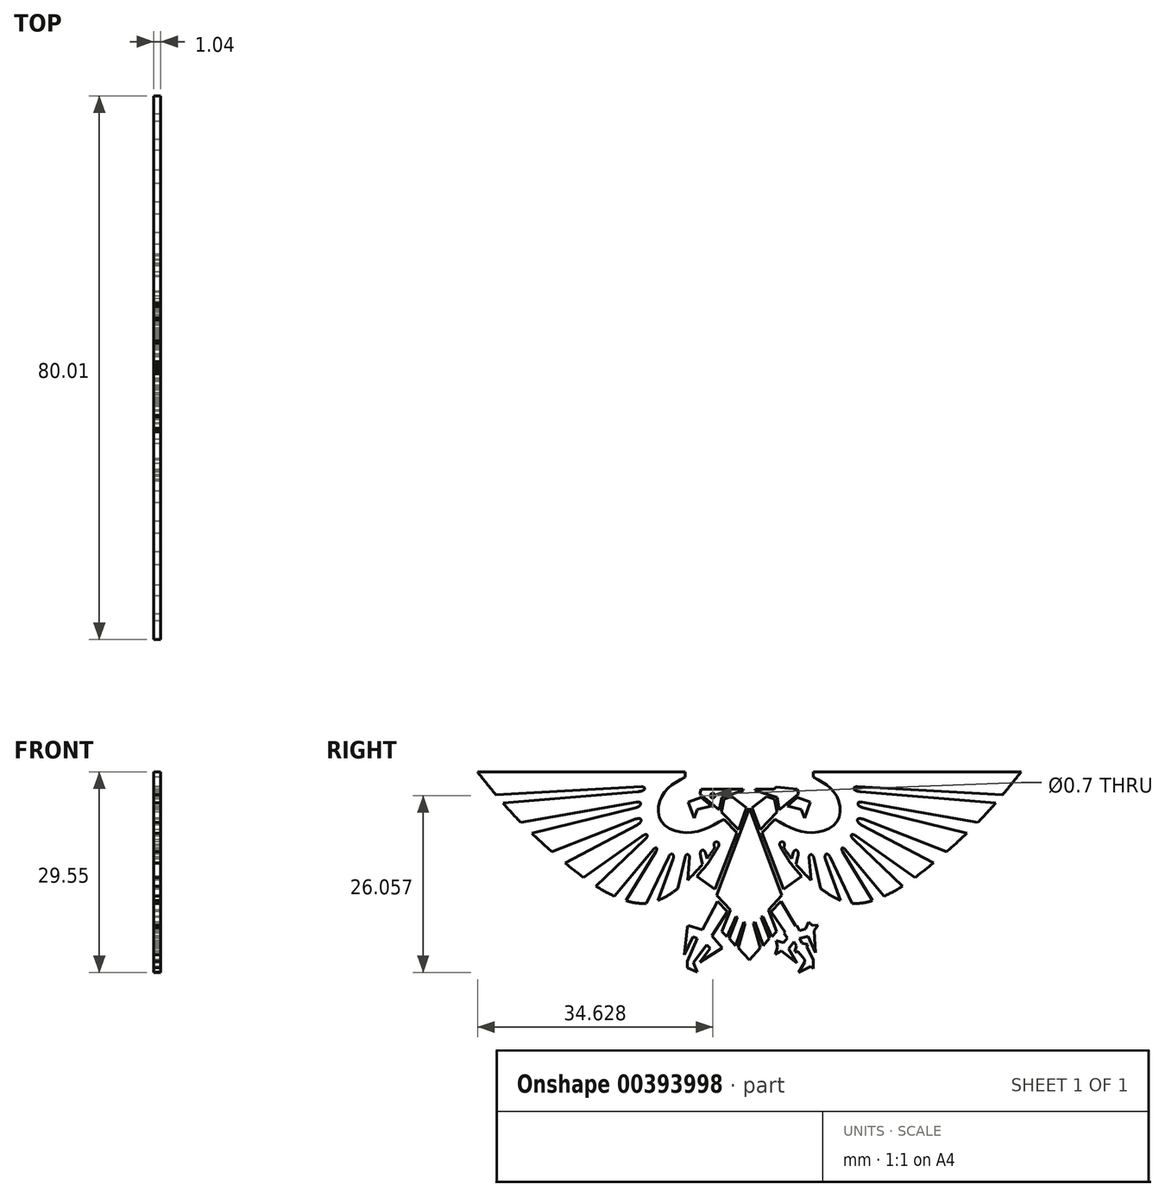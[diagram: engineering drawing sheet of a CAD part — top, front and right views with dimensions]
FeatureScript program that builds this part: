
annotation { "Feature Type Name" : "Feature", "Feature Type Description" : "" }
export const myFeature = defineFeature(function(context is Context, id is Id, definition is map)
    precondition{}
    {
        {
            var Q0;
            Q0=qCreatedBy(makeId("Right.planeOp"),FACE);
            var sketch = newSketch(context, id + "F0", { "sketchPlane" : qUnion([Q0])});
            skLineSegment(sketch, "E0", {"start": v(-102.5, 27.31) * mm, "end": v(-14.2, 27.31) * mm});
            skLineSegment(sketch, "E1", {"start": v(-14.2, 27.31) * mm, "end": v(-14.2, 25.13) * mm});
            skFitSpline(sketch, "E2", {"points": [v(-14.2, 25.13) * mm, v(-23.72, 17.79) * mm, v(-24.31, 6.28) * mm, v(-11.99, 1.57) * mm, v(2.22, 7.22) * mm], "startDerivative": vector(-46.05, -24.12) * mm, "endDerivative": vector(50.08, 29.12) * mm});
            skLineSegment(sketch, "E3", {"start": v(2.22, 7.22) * mm, "end": v(7.69, 1.39) * mm});
            skLineSegment(sketch, "E4", {"start": v(7.69, 1.39) * mm, "end": v(-1.6, -22.65) * mm});
            skLineSegment(sketch, "E5", {"start": v(-1.6, -22.65) * mm, "end": v(-9.22, -17.02) * mm});
            skLineSegment(sketch, "E6", {"start": v(-7.37, 16.54) * mm, "end": v(-12.93, 14.54) * mm});
            skLineSegment(sketch, "E7", {"start": v(-12.93, 14.54) * mm, "end": v(-10.45, 7.62) * mm});
            skLineSegment(sketch, "E8", {"start": v(-10.45, 7.62) * mm, "end": v(-9.02, 11.32) * mm});
            skLineSegment(sketch, "E9", {"start": v(-9.02, 11.32) * mm, "end": v(-3.1, 12.9) * mm});
            skLineSegment(sketch, "E10", {"start": v(-3.1, 12.9) * mm, "end": v(-7.37, 16.54) * mm});
            skLineSegment(sketch, "E11", {"start": v(-7.97, 17.99) * mm, "end": v(0.28, 11.15) * mm});
            skLineSegment(sketch, "E12", {"start": v(0.28, 11.15) * mm, "end": v(1.28, 16.54) * mm});
            skLineSegment(sketch, "E13", {"start": v(1.28, 16.54) * mm, "end": v(10.59, 19.35) * mm});
            skLineSegment(sketch, "E14", {"start": v(10.59, 19.35) * mm, "end": v(10.42, 19.92) * mm});
            skLineSegment(sketch, "E15", {"start": v(10.42, 19.92) * mm, "end": v(-7.37, 19.92) * mm});
            skLineSegment(sketch, "E16", {"start": v(-7.37, 19.92) * mm, "end": v(-7.97, 17.99) * mm});
            skLineSegment(sketch, "E17", {"start": v(1.22, 10.26) * mm, "end": v(2.3, 15.81) * mm});
            skLineSegment(sketch, "E18", {"start": v(2.3, 15.81) * mm, "end": v(5.56, 16.82) * mm});
            skLineSegment(sketch, "E19", {"start": v(5.56, 16.82) * mm, "end": v(11.86, 12.16) * mm});
            skLineSegment(sketch, "E20", {"start": v(11.86, 12.16) * mm, "end": v(8.46, 2.82) * mm});
            skLineSegment(sketch, "E21", {"start": v(8.46, 2.82) * mm, "end": v(1.22, 10.26) * mm});
            skLineSegment(sketch, "E22", {"start": v(13.02, 11.9) * mm, "end": v(-0.86, -25.12) * mm});
            skLineSegment(sketch, "E23", {"start": v(-0.86, -25.12) * mm, "end": v(4.96, -31.43) * mm});
            skLineSegment(sketch, "E24", {"start": v(4.96, -31.43) * mm, "end": v(1.4, -40.46) * mm});
            skLineSegment(sketch, "E25", {"start": v(1.4, -40.46) * mm, "end": v(3.5, -42.79) * mm});
            skLineSegment(sketch, "E26", {"start": v(3.5, -42.79) * mm, "end": v(7.33, -34.11) * mm});
            skLineSegment(sketch, "E27", {"start": v(7.33, -34.11) * mm, "end": v(7.98, -34.4) * mm});
            skLineSegment(sketch, "E28", {"start": v(7.98, -34.4) * mm, "end": v(4.45, -43.45) * mm});
            skLineSegment(sketch, "E29", {"start": v(4.45, -43.45) * mm, "end": v(7.17, -46.54) * mm});
            skLineSegment(sketch, "E30", {"start": v(7.17, -46.54) * mm, "end": v(10.62, -36.41) * mm});
            skLineSegment(sketch, "E31", {"start": v(10.62, -36.41) * mm, "end": v(11.23, -36.98) * mm});
            skLineSegment(sketch, "E32", {"start": v(11.23, -36.98) * mm, "end": v(8.31, -47.45) * mm});
            skLineSegment(sketch, "E33", {"start": v(13.02, 11.9) * mm, "end": v(13.02, -55.3) * mm, "construction": true});
            skLineSegment(sketch, "E34", {"start": v(8.31, -47.45) * mm, "end": v(13.02, -52.66) * mm});
            skLineSegment(sketch, "E35", {"start": v(3.82, -32) * mm, "end": v(-0.39, -27.68) * mm});
            skLineSegment(sketch, "E36", {"start": v(-0.39, -27.68) * mm, "end": v(-6.96, -39.7) * mm});
            skLineSegment(sketch, "E37", {"start": v(-6.96, -39.7) * mm, "end": v(-12.97, -37.89) * mm});
            skLineSegment(sketch, "E38", {"start": v(-12.97, -37.89) * mm, "end": v(-13.27, -38.87) * mm});
            skLineSegment(sketch, "E39", {"start": v(-13.27, -38.87) * mm, "end": v(-14.6, -50.48) * mm});
            skLineSegment(sketch, "E40", {"start": v(-14.6, -50.48) * mm, "end": v(-10.87, -42.73) * mm});
            skLineSegment(sketch, "E41", {"start": v(-10.87, -42.73) * mm, "end": v(-9.13, -43.42) * mm});
            skLineSegment(sketch, "E42", {"start": v(-9.13, -43.42) * mm, "end": v(-13.27, -53.25) * mm});
            skLineSegment(sketch, "E43", {"start": v(-13.27, -53.25) * mm, "end": v(-13.27, -55.86) * mm});
            skLineSegment(sketch, "E44", {"start": v(-13.27, -55.86) * mm, "end": v(-9.01, -57.84) * mm});
            skLineSegment(sketch, "E45", {"start": v(-9.01, -57.84) * mm, "end": v(-10.7, -53.82) * mm});
            skLineSegment(sketch, "E46", {"start": v(-10.7, -53.82) * mm, "end": v(-5.08, -46.23) * mm});
            skLineSegment(sketch, "E47", {"start": v(-5.08, -46.23) * mm, "end": v(-3.53, -47.66) * mm});
            skLineSegment(sketch, "E48", {"start": v(-3.53, -47.66) * mm, "end": v(-7.97, -53.52) * mm});
            skLineSegment(sketch, "E49", {"start": v(-7.97, -53.52) * mm, "end": v(1.45, -47.42) * mm});
            skLineSegment(sketch, "E50", {"start": v(1.45, -47.42) * mm, "end": v(-2.85, -42.44) * mm});
            skLineSegment(sketch, "E51", {"start": v(-2.85, -42.44) * mm, "end": v(3.82, -32) * mm});
            skLineSegment(sketch, "E52.MirrorCS", {"start": v(13.02, 11.9) * mm, "end": v(26.9, -25.12) * mm});
            skLineSegment(sketch, "E53.MirrorCS", {"start": v(26.9, -25.12) * mm, "end": v(21.08, -31.43) * mm});
            skLineSegment(sketch, "E54.MirrorCS", {"start": v(21.08, -31.43) * mm, "end": v(24.64, -40.46) * mm});
            skLineSegment(sketch, "E55.MirrorCS", {"start": v(24.64, -40.46) * mm, "end": v(22.55, -42.79) * mm});
            skLineSegment(sketch, "E56.MirrorCS", {"start": v(22.55, -42.79) * mm, "end": v(18.72, -34.11) * mm});
            skLineSegment(sketch, "E57.MirrorCS", {"start": v(18.07, -34.4) * mm, "end": v(21.6, -43.45) * mm});
            skLineSegment(sketch, "E58.MirrorCS", {"start": v(18.72, -34.11) * mm, "end": v(18.07, -34.4) * mm});
            skLineSegment(sketch, "E59.MirrorCS", {"start": v(21.6, -43.45) * mm, "end": v(18.88, -46.54) * mm});
            skLineSegment(sketch, "E60.MirrorCS", {"start": v(18.88, -46.54) * mm, "end": v(15.43, -36.41) * mm});
            skLineSegment(sketch, "E61.MirrorCS", {"start": v(15.43, -36.41) * mm, "end": v(14.82, -36.98) * mm});
            skLineSegment(sketch, "E62.MirrorCS", {"start": v(14.82, -36.98) * mm, "end": v(17.73, -47.45) * mm});
            skLineSegment(sketch, "E63.MirrorCS", {"start": v(17.73, -47.45) * mm, "end": v(13.02, -52.66) * mm});
            skLineSegment(sketch, "E64.MirrorCS", {"start": v(17.58, 2.82) * mm, "end": v(24.83, 10.26) * mm});
            skLineSegment(sketch, "E65.MirrorCS", {"start": v(24.83, 10.26) * mm, "end": v(23.75, 15.81) * mm});
            skLineSegment(sketch, "E66.MirrorCS", {"start": v(23.75, 15.81) * mm, "end": v(20.49, 16.82) * mm});
            skLineSegment(sketch, "E67.MirrorCS", {"start": v(20.49, 16.82) * mm, "end": v(14.19, 12.16) * mm});
            skLineSegment(sketch, "E68.MirrorCS", {"start": v(14.19, 12.16) * mm, "end": v(17.58, 2.82) * mm});
            skLineSegment(sketch, "E69.MirrorCS", {"start": v(27.63, -22.65) * mm, "end": v(35.27, -17.02) * mm});
            skLineSegment(sketch, "E70.MirrorCS", {"start": v(18.36, 1.39) * mm, "end": v(27.63, -22.65) * mm});
            skLineSegment(sketch, "E71.MirrorCS", {"start": v(23.82, 7.22) * mm, "end": v(18.36, 1.39) * mm});
            skFitSpline(sketch, "E72.MirrorCS", {"points": [v(40.24, 25.13) * mm, v(49.76, 17.79) * mm, v(50.36, 6.28) * mm, v(38.03, 1.57) * mm, v(23.82, 7.22) * mm], "startDerivative": vector(46.05, -24.12) * mm, "endDerivative": vector(-50.08, 29.12) * mm});
            skLineSegment(sketch, "E73.MirrorCS", {"start": v(40.24, 27.31) * mm, "end": v(40.24, 25.13) * mm});
            skLineSegment(sketch, "E74.MirrorCS", {"start": v(128.54, 27.31) * mm, "end": v(40.24, 27.31) * mm});
            skLineSegment(sketch, "E75.MirrorCS", {"start": v(33.41, 16.54) * mm, "end": v(38.98, 14.54) * mm});
            skLineSegment(sketch, "E76.MirrorCS", {"start": v(38.98, 14.54) * mm, "end": v(36.5, 7.62) * mm});
            skLineSegment(sketch, "E77.MirrorCS", {"start": v(36.5, 7.62) * mm, "end": v(35.06, 11.32) * mm});
            skLineSegment(sketch, "E78.MirrorCS", {"start": v(35.06, 11.32) * mm, "end": v(29.15, 12.9) * mm});
            skLineSegment(sketch, "E79.MirrorCS", {"start": v(29.15, 12.9) * mm, "end": v(33.41, 16.54) * mm});
            skLineSegment(sketch, "E80.MirrorCS", {"start": v(34.02, 17.99) * mm, "end": v(25.76, 11.15) * mm});
            skLineSegment(sketch, "E81.MirrorCS", {"start": v(33.41, 19.92) * mm, "end": v(34.02, 17.99) * mm});
            skLineSegment(sketch, "E82.MirrorCS", {"start": v(15.63, 19.92) * mm, "end": v(23.49, 19.92) * mm});
            skLineSegment(sketch, "E83.MirrorCS", {"start": v(24.77, 16.54) * mm, "end": v(15.46, 19.35) * mm});
            skLineSegment(sketch, "E84.MirrorCS", {"start": v(25.76, 11.15) * mm, "end": v(24.77, 16.54) * mm});
            skLineSegment(sketch, "E85.MirrorCS", {"start": v(15.46, 19.35) * mm, "end": v(15.63, 19.92) * mm});
            skLineSegment(sketch, "E86.MirrorCS", {"start": v(22.23, -32) * mm, "end": v(26.43, -27.68) * mm});
            skFitSpline(sketch, "E87", {"points": [v(-102.5, 27.31) * mm, v(-84.01, 5.77) * mm, v(-57.46, -17.55) * mm, v(-44.3, -25.5) * mm, v(-30.65, -28.53) * mm, v(-17.36, -22.24) * mm, v(-7.17, -12.27) * mm, v(-1.68, -5.11) * mm], "startDerivative": vector(92.01, -116.2) * mm, "endDerivative": vector(49.15, 67.82) * mm});
            skFitSpline(sketch, "E88", {"points": [v(-9.22, -17.02) * mm, v(-4.13, -10.84) * mm, v(0, -4.1) * mm], "startDerivative": vector(10.62, 12) * mm, "endDerivative": vector(7.82, 13.82) * mm});
            skLineSegment(sketch, "E89", {"start": v(-94.7, 17.65) * mm, "end": v(-32.83, 21) * mm});
            skLineSegment(sketch, "E90", {"start": v(-91.68, 14.1) * mm, "end": v(-34.42, 18.9) * mm});
            skLineSegment(sketch, "E91", {"start": v(-84.01, 5.77) * mm, "end": v(-34.98, 14.5) * mm});
            skLineSegment(sketch, "E92", {"start": v(-79.38, 1.2) * mm, "end": v(-35.2, 12.18) * mm});
            skLineSegment(sketch, "E93", {"start": v(-70.86, -6.6) * mm, "end": v(-35.27, 7.25) * mm});
            skLineSegment(sketch, "E94", {"start": v(-65.27, -11.36) * mm, "end": v(-34.5, 4.85) * mm});
            skLineSegment(sketch, "E95", {"start": v(-57.46, -17.55) * mm, "end": v(-32.55, 0) * mm});
            skLineSegment(sketch, "E96", {"start": v(-52.22, -21.21) * mm, "end": v(-31.4, -1.44) * mm});
            skLineSegment(sketch, "E97", {"start": v(-44.3, -25.5) * mm, "end": v(-27.61, -5.6) * mm});
            skLineSegment(sketch, "E98", {"start": v(-39.4, -27.39) * mm, "end": v(-26.61, -6.52) * mm});
            skLineSegment(sketch, "E99", {"start": v(-30.65, -28.53) * mm, "end": v(-21.26, -8.78) * mm});
            skLineSegment(sketch, "E100", {"start": v(-25.75, -27.3) * mm, "end": v(-19.33, -9.7) * mm});
            skLineSegment(sketch, "E101", {"start": v(-17.36, -22.24) * mm, "end": v(-14.31, -9.03) * mm});
            skLineSegment(sketch, "E102", {"start": v(-13.21, -18.67) * mm, "end": v(-12.44, -8.8) * mm});
            skLineSegment(sketch, "E103", {"start": v(-6.93, -11.98) * mm, "end": v(-7.63, -8.57) * mm});
            skLineSegment(sketch, "E104", {"start": v(-4.95, -9.52) * mm, "end": v(-5.58, -7.1) * mm});
            skLineSegment(sketch, "E105", {"start": v(-1.68, -5.11) * mm, "end": v(-1.96, -3.58) * mm});
            skCircle(sketch, "E106", {"center": v(-2.5, 17.22) * mm, "radius": 1 * mm});
            skPoint(sketch, "E106.first.point", {"position": v(-3.51, 17.29) * mm});
            skPoint(sketch, "E106.second.point", {"position": v(-2.03, 18.11) * mm});
            skPoint(sketch, "E106.third.point", {"position": v(-2.18, 16.27) * mm});
            skFitSpline(sketch, "E107", {"points": [v(-32.83, 21) * mm, v(-31.8, 20.85) * mm, v(-31.38, 20.36) * mm, v(-31.93, 19.5) * mm, v(-34.42, 18.9) * mm], "startDerivative": vector(5.47, 0.3) * mm, "endDerivative": vector(-7.95, -0.9) * mm});
            skFitSpline(sketch, "E108", {"points": [v(-34.98, 14.5) * mm, v(-33.85, 14.52) * mm, v(-33.2, 14.13) * mm, v(-33.7, 12.8) * mm, v(-35.2, 12.18) * mm], "startDerivative": vector(6.77, 1.18) * mm, "endDerivative": vector(-4.8, -1.36) * mm});
            skFitSpline(sketch, "E109", {"points": [v(-35.27, 7.25) * mm, v(-33.14, 7.34) * mm, v(-34.5, 4.85) * mm], "startDerivative": vector(5.17, 2.1) * mm, "endDerivative": vector(-8.48, -4.87) * mm});
            skFitSpline(sketch, "E110", {"points": [v(-32.55, 0) * mm, v(-30.48, 0.65) * mm, v(-31.4, -1.44) * mm], "startDerivative": vector(4.99, 3.9) * mm, "endDerivative": vector(-6.03, -5.2) * mm});
            skFitSpline(sketch, "E111", {"points": [v(-27.61, -5.6) * mm, v(-26.46, -4.98) * mm, v(-26.61, -6.52) * mm], "startDerivative": vector(2.73, 3.38) * mm, "endDerivative": vector(-2.12, -3.5) * mm});
            skFitSpline(sketch, "E112", {"points": [v(-21.26, -8.78) * mm, v(-19.64, -7.62) * mm, v(-19.33, -9.7) * mm], "startDerivative": vector(2.73, 5.71) * mm, "endDerivative": vector(-1.8, -5.35) * mm});
            skFitSpline(sketch, "E113", {"points": [v(-14.31, -9.03) * mm, v(-13.28, -7.78) * mm, v(-12.44, -8.8) * mm], "startDerivative": vector(1.13, 4.45) * mm, "endDerivative": vector(-0.23, -3.85) * mm});
            skFitSpline(sketch, "E114", {"points": [v(-7.63, -8.57) * mm, v(-7.2, -6.02) * mm, v(-5.58, -7.1) * mm], "startDerivative": vector(-1.5, 7.33) * mm, "endDerivative": vector(1.7, -6.93) * mm});
            skFitSpline(sketch, "E115", {"points": [v(-1.96, -3.58) * mm, v(-0.79, -2.4) * mm, v(0, -4.1) * mm], "startDerivative": vector(-0.6, 5.41) * mm, "endDerivative": vector(-2.7, -5.49) * mm});
            skLineSegment(sketch, "E116", {"start": v(23.49, 19.92) * mm, "end": v(24.42, 20.82) * mm});
            skLineSegment(sketch, "E117", {"start": v(24.42, 20.82) * mm, "end": v(33.41, 19.92) * mm});
            skPoint(sketch, "E118.orphan", {"position": v(33.41, 19.92) * mm});
            skLineSegment(sketch, "E119", {"start": v(22.23, -32) * mm, "end": v(28.33, -40.87) * mm});
            skLineSegment(sketch, "E120", {"start": v(28.33, -40.87) * mm, "end": v(27.81, -41.22) * mm});
            skLineSegment(sketch, "E121", {"start": v(27.81, -41.22) * mm, "end": v(29.23, -43.28) * mm});
            skLineSegment(sketch, "E122", {"start": v(29.23, -43.28) * mm, "end": v(27.54, -45.32) * mm});
            skLineSegment(sketch, "E123", {"start": v(27.54, -45.32) * mm, "end": v(24.43, -44.4) * mm});
            skLineSegment(sketch, "E124", {"start": v(24.43, -44.4) * mm, "end": v(25.03, -47.15) * mm});
            skLineSegment(sketch, "E125", {"start": v(25.03, -47.15) * mm, "end": v(24.15, -50.23) * mm});
            skLineSegment(sketch, "E126", {"start": v(24.15, -50.23) * mm, "end": v(26.7, -48.85) * mm});
            skLineSegment(sketch, "E127", {"start": v(26.7, -48.85) * mm, "end": v(33.32, -53.9) * mm});
            skLineSegment(sketch, "E128", {"start": v(33.32, -53.9) * mm, "end": v(29.8, -47.92) * mm});
            skLineSegment(sketch, "E129", {"start": v(29.8, -47.92) * mm, "end": v(32, -44.9) * mm});
            skLineSegment(sketch, "E130", {"start": v(32, -44.9) * mm, "end": v(33.05, -46.67) * mm});
            skLineSegment(sketch, "E131", {"start": v(33.05, -46.67) * mm, "end": v(32.41, -49.16) * mm});
            skLineSegment(sketch, "E132", {"start": v(32.41, -49.16) * mm, "end": v(33.88, -49.16) * mm});
            skLineSegment(sketch, "E133", {"start": v(33.88, -49.16) * mm, "end": v(36.62, -52.5) * mm});
            skLineSegment(sketch, "E134", {"start": v(36.62, -52.5) * mm, "end": v(36.62, -53.46) * mm});
            skLineSegment(sketch, "E135", {"start": v(36.62, -53.46) * mm, "end": v(34.03, -58.03) * mm});
            skLineSegment(sketch, "E136", {"start": v(34.03, -58.03) * mm, "end": v(39.19, -55.44) * mm});
            skLineSegment(sketch, "E137", {"start": v(39.19, -55.44) * mm, "end": v(40.24, -56.26) * mm});
            skLineSegment(sketch, "E138", {"start": v(40.24, -56.26) * mm, "end": v(40.24, -52.53) * mm});
            skLineSegment(sketch, "E139", {"start": v(40.24, -52.53) * mm, "end": v(37.47, -47.06) * mm});
            skLineSegment(sketch, "E140", {"start": v(37.47, -47.06) * mm, "end": v(37.86, -45.95) * mm});
            skLineSegment(sketch, "E141", {"start": v(37.86, -45.95) * mm, "end": v(35.51, -45.42) * mm});
            skLineSegment(sketch, "E142", {"start": v(35.51, -45.42) * mm, "end": v(34.32, -43.46) * mm});
            skLineSegment(sketch, "E143", {"start": v(34.32, -43.46) * mm, "end": v(37.98, -42.57) * mm});
            skLineSegment(sketch, "E144", {"start": v(37.98, -42.57) * mm, "end": v(41.15, -49.58) * mm});
            skLineSegment(sketch, "E145", {"start": v(41.15, -49.58) * mm, "end": v(40.52, -40.12) * mm});
            skLineSegment(sketch, "E146", {"start": v(40.52, -40.12) * mm, "end": v(42.28, -37.71) * mm});
            skLineSegment(sketch, "E147", {"start": v(42.28, -37.71) * mm, "end": v(39.85, -37.91) * mm});
            skLineSegment(sketch, "E148", {"start": v(39.85, -37.91) * mm, "end": v(38.17, -36.5) * mm});
            skLineSegment(sketch, "E149", {"start": v(38.17, -36.5) * mm, "end": v(36.86, -39.45) * mm});
            skLineSegment(sketch, "E150", {"start": v(36.86, -39.45) * mm, "end": v(34.44, -40.16) * mm});
            skLineSegment(sketch, "E151", {"start": v(34.44, -40.16) * mm, "end": v(33.2, -37.9) * mm});
            skLineSegment(sketch, "E152", {"start": v(33.2, -37.9) * mm, "end": v(32.78, -38.12) * mm});
            skLineSegment(sketch, "E153", {"start": v(32.78, -38.12) * mm, "end": v(26.43, -27.68) * mm});
            skFitSpline(sketch, "E154.MirrorCS", {"points": [v(35.27, -17.02) * mm, v(30.17, -10.84) * mm, v(26.04, -4.1) * mm], "startDerivative": vector(-10.62, 12) * mm, "endDerivative": vector(-7.82, 13.82) * mm});
            skFitSpline(sketch, "E155.MirrorCS", {"points": [v(28, -3.58) * mm, v(26.83, -2.4) * mm, v(26.04, -4.1) * mm], "startDerivative": vector(0.6, 5.41) * mm, "endDerivative": vector(2.7, -5.49) * mm});
            skLineSegment(sketch, "E156.MirrorCS", {"start": v(27.72, -5.11) * mm, "end": v(28, -3.58) * mm});
            skFitSpline(sketch, "E157.MirrorCS", {"points": [v(128.54, 27.31) * mm, v(110.06, 5.77) * mm, v(83.5, -17.55) * mm, v(70.35, -25.5) * mm, v(56.7, -28.53) * mm, v(43.4, -22.24) * mm, v(33.22, -12.27) * mm, v(27.72, -5.11) * mm], "startDerivative": vector(-92.01, -116.2) * mm, "endDerivative": vector(-49.15, 67.82) * mm});
            skLineSegment(sketch, "E158.MirrorCS", {"start": v(31, -9.52) * mm, "end": v(31.63, -7.1) * mm});
            skFitSpline(sketch, "E159.MirrorCS", {"points": [v(33.67, -8.57) * mm, v(33.25, -6.02) * mm, v(31.63, -7.1) * mm], "startDerivative": vector(1.5, 7.33) * mm, "endDerivative": vector(-1.7, -6.93) * mm});
            skLineSegment(sketch, "E160.MirrorCS", {"start": v(32.97, -11.98) * mm, "end": v(33.67, -8.57) * mm});
            skLineSegment(sketch, "E161.MirrorCS", {"start": v(39.26, -18.67) * mm, "end": v(38.49, -8.8) * mm});
            skFitSpline(sketch, "E162.MirrorCS", {"points": [v(40.36, -9.03) * mm, v(39.33, -7.78) * mm, v(38.49, -8.8) * mm], "startDerivative": vector(-1.13, 4.45) * mm, "endDerivative": vector(0.23, -3.85) * mm});
            skLineSegment(sketch, "E163.MirrorCS", {"start": v(43.4, -22.24) * mm, "end": v(40.36, -9.03) * mm});
            skLineSegment(sketch, "E164.MirrorCS", {"start": v(51.8, -27.3) * mm, "end": v(45.37, -9.7) * mm});
            skFitSpline(sketch, "E165.MirrorCS", {"points": [v(47.3, -8.78) * mm, v(45.68, -7.62) * mm, v(45.37, -9.7) * mm], "startDerivative": vector(-2.73, 5.71) * mm, "endDerivative": vector(1.8, -5.35) * mm});
            skLineSegment(sketch, "E166.MirrorCS", {"start": v(56.7, -28.53) * mm, "end": v(47.3, -8.78) * mm});
            skLineSegment(sketch, "E167.MirrorCS", {"start": v(65.44, -27.39) * mm, "end": v(52.66, -6.52) * mm});
            skLineSegment(sketch, "E168.MirrorCS", {"start": v(70.35, -25.5) * mm, "end": v(53.66, -5.6) * mm});
            skFitSpline(sketch, "E169.MirrorCS", {"points": [v(53.66, -5.6) * mm, v(52.5, -4.98) * mm, v(52.66, -6.52) * mm], "startDerivative": vector(-2.73, 3.38) * mm, "endDerivative": vector(2.12, -3.5) * mm});
            skLineSegment(sketch, "E170.MirrorCS", {"start": v(78.26, -21.21) * mm, "end": v(57.44, -1.44) * mm});
            skFitSpline(sketch, "E171.MirrorCS", {"points": [v(58.6, 0) * mm, v(56.53, 0.65) * mm, v(57.44, -1.44) * mm], "startDerivative": vector(-4.99, 3.9) * mm, "endDerivative": vector(6.03, -5.2) * mm});
            skLineSegment(sketch, "E172.MirrorCS", {"start": v(83.5, -17.55) * mm, "end": v(58.6, 0) * mm});
            skLineSegment(sketch, "E173.MirrorCS", {"start": v(91.32, -11.36) * mm, "end": v(60.54, 4.85) * mm});
            skFitSpline(sketch, "E174.MirrorCS", {"points": [v(61.31, 7.25) * mm, v(59.19, 7.34) * mm, v(60.54, 4.85) * mm], "startDerivative": vector(-5.17, 2.1) * mm, "endDerivative": vector(8.48, -4.87) * mm});
            skLineSegment(sketch, "E175.MirrorCS", {"start": v(96.9, -6.6) * mm, "end": v(61.31, 7.25) * mm});
            skLineSegment(sketch, "E176.MirrorCS", {"start": v(105.43, 1.2) * mm, "end": v(61.24, 12.18) * mm});
            skLineSegment(sketch, "E177.MirrorCS", {"start": v(110.06, 5.77) * mm, "end": v(61.02, 14.5) * mm});
            skLineSegment(sketch, "E178.MirrorCS", {"start": v(117.73, 14.1) * mm, "end": v(60.46, 18.9) * mm});
            skFitSpline(sketch, "E179.MirrorCS", {"points": [v(58.88, 21) * mm, v(57.84, 20.85) * mm, v(57.42, 20.36) * mm, v(57.97, 19.5) * mm, v(60.46, 18.9) * mm], "startDerivative": vector(-5.47, 0.3) * mm, "endDerivative": vector(7.95, -0.9) * mm});
            skLineSegment(sketch, "E180.MirrorCS", {"start": v(120.75, 17.65) * mm, "end": v(58.88, 21) * mm});
            skFitSpline(sketch, "E181.MirrorCS", {"points": [v(61.02, 14.5) * mm, v(59.9, 14.52) * mm, v(59.25, 14.13) * mm, v(59.74, 12.8) * mm, v(61.24, 12.18) * mm], "startDerivative": vector(-6.77, 1.18) * mm, "endDerivative": vector(4.8, -1.36) * mm});
            skSolve(sketch);
        }
        {
            var Q0;
            Q0=makeQuery(id+"F0.imprint","IMPRINT",FACE,{"disambiguationData":[TD([[makeQuery(id+"F0.imprint","IMPRINT",EDGE,{"derivedFrom":sQuery(id+"F0.wireOp",EDGE,"E22")}),1.0]])]});
            var Q1;
            {var subQ14=sQuery(id+"F0.wireOp",EDGE,"E0");Q1=makeQuery(id+"F0.imprint","IMPRINT",FACE,{"disambiguationData":[TD([[makeQuery(id+"F0.imprint","IMPRINT",EDGE,{"derivedFrom":subQ14}),-1.0]])]});}
            var Q2;
            Q2=makeQuery(id+"F0.imprint","IMPRINT",FACE,{"disambiguationData":[TD([[makeQuery(id+"F0.imprint","IMPRINT",EDGE,{"derivedFrom":sQuery(id+"F0.wireOp",EDGE,"E17")}),-1.0]])]});
            var Q3;
            Q3=makeQuery(id+"F0.imprint","IMPRINT",FACE,{"disambiguationData":[TD([[makeQuery(id+"F0.imprint","IMPRINT",EDGE,{"derivedFrom":sQuery(id+"F0.wireOp",EDGE,"E11")}),1.0]])]});
            var Q4;
            Q4=makeQuery(id+"F0.imprint","IMPRINT",FACE,{"disambiguationData":[TD([[makeQuery(id+"F0.imprint","IMPRINT",EDGE,{"derivedFrom":sQuery(id+"F0.wireOp",EDGE,"E6")}),1.0]])]});
            var Q5;
            Q5=makeQuery(id+"F0.imprint","IMPRINT",FACE,{"disambiguationData":[TD([[makeQuery(id+"F0.imprint","IMPRINT",EDGE,{"derivedFrom":sQuery(id+"F0.wireOp",EDGE,"E64.MirrorCS")}),1.0]])]});
            var Q6;
            Q6=makeQuery(id+"F0.imprint","IMPRINT",FACE,{"disambiguationData":[TD([[makeQuery(id+"F0.imprint","IMPRINT",EDGE,{"derivedFrom":sQuery(id+"F0.wireOp",EDGE,"E75.MirrorCS")}),-1.0]])]});
            var Q7;
            Q7=makeQuery(id+"F0.imprint","IMPRINT",FACE,{"disambiguationData":[TD([[makeQuery(id+"F0.imprint","IMPRINT",EDGE,{"derivedFrom":sQuery(id+"F0.wireOp",EDGE,"E69.MirrorCS")}),1.0]])]});
            var Q8;
            Q8=makeQuery(id+"F0.imprint","IMPRINT",FACE,{"disambiguationData":[TD([[makeQuery(id+"F0.imprint","IMPRINT",EDGE,{"derivedFrom":sQuery(id+"F0.wireOp",EDGE,"E80.MirrorCS")}),-1.0]])]});
            var Q9;
            Q9=makeQuery(id+"F0.imprint","IMPRINT",FACE,{"disambiguationData":[TD([[makeQuery(id+"F0.imprint","IMPRINT",EDGE,{"derivedFrom":sQuery(id+"F0.wireOp",EDGE,"E35")}),1.0]])]});
            var Q10;
            Q10=makeQuery(id+"F0.imprint","IMPRINT",FACE,{"disambiguationData":[TD([[makeQuery(id+"F0.imprint","IMPRINT",EDGE,{"derivedFrom":sQuery(id+"F0.wireOp",EDGE,"E86.MirrorCS")}),-1.0]])]});
            extrude(context, id + "F1", {"entities" : qUnion([Q0, Q1, Q2, Q3, Q4, Q5, Q6, Q7, Q8, Q9, Q10]), "depth" : 3 * mm});
        }
        {
            var Q0;
            Q0=makeQuery(id+"F1.opExtrude","SWEPT_BODY",BODY,{"disambiguationData":[OSD([sQuery(id+"F0.wireOp",EDGE,"E86.MirrorCS"),sQuery(id+"F0.wireOp",EDGE,"E119"),sQuery(id+"F0.wireOp",EDGE,"E120"),sQuery(id+"F0.wireOp",EDGE,"E121"),sQuery(id+"F0.wireOp",EDGE,"E122"),sQuery(id+"F0.wireOp",EDGE,"E123"),sQuery(id+"F0.wireOp",EDGE,"E124"),sQuery(id+"F0.wireOp",EDGE,"E125"),sQuery(id+"F0.wireOp",EDGE,"E126"),sQuery(id+"F0.wireOp",EDGE,"E127"),sQuery(id+"F0.wireOp",EDGE,"E128"),sQuery(id+"F0.wireOp",EDGE,"E129"),sQuery(id+"F0.wireOp",EDGE,"E130"),sQuery(id+"F0.wireOp",EDGE,"E131"),sQuery(id+"F0.wireOp",EDGE,"E132"),sQuery(id+"F0.wireOp",EDGE,"E133"),sQuery(id+"F0.wireOp",EDGE,"E134"),sQuery(id+"F0.wireOp",EDGE,"E135"),sQuery(id+"F0.wireOp",EDGE,"E136"),sQuery(id+"F0.wireOp",EDGE,"E137"),sQuery(id+"F0.wireOp",EDGE,"E138"),sQuery(id+"F0.wireOp",EDGE,"E139"),sQuery(id+"F0.wireOp",EDGE,"E140"),sQuery(id+"F0.wireOp",EDGE,"E141"),sQuery(id+"F0.wireOp",EDGE,"E142"),sQuery(id+"F0.wireOp",EDGE,"E143"),sQuery(id+"F0.wireOp",EDGE,"E144"),sQuery(id+"F0.wireOp",EDGE,"E145"),sQuery(id+"F0.wireOp",EDGE,"E146"),sQuery(id+"F0.wireOp",EDGE,"E147"),sQuery(id+"F0.wireOp",EDGE,"E148"),sQuery(id+"F0.wireOp",EDGE,"E149"),sQuery(id+"F0.wireOp",EDGE,"E150"),sQuery(id+"F0.wireOp",EDGE,"E151"),sQuery(id+"F0.wireOp",EDGE,"E152"),sQuery(id+"F0.wireOp",EDGE,"E153")])]});
            var Q1;
            Q1=makeQuery(id+"F1.opExtrude","SWEPT_BODY",BODY,{"disambiguationData":[OSD([sQuery(id+"F0.wireOp",EDGE,"E0"),sQuery(id+"F0.wireOp",EDGE,"E1"),sQuery(id+"F0.wireOp",EDGE,"E2"),sQuery(id+"F0.wireOp",EDGE,"E3"),sQuery(id+"F0.wireOp",EDGE,"E4"),sQuery(id+"F0.wireOp",EDGE,"E5"),sQuery(id+"F0.wireOp",EDGE,"E87"),sQuery(id+"F0.wireOp",EDGE,"E88"),sQuery(id+"F0.wireOp",EDGE,"E89"),sQuery(id+"F0.wireOp",EDGE,"E90"),sQuery(id+"F0.wireOp",EDGE,"E91"),sQuery(id+"F0.wireOp",EDGE,"E92"),sQuery(id+"F0.wireOp",EDGE,"E93"),sQuery(id+"F0.wireOp",EDGE,"E94"),sQuery(id+"F0.wireOp",EDGE,"E95"),sQuery(id+"F0.wireOp",EDGE,"E96"),sQuery(id+"F0.wireOp",EDGE,"E97"),sQuery(id+"F0.wireOp",EDGE,"E98"),sQuery(id+"F0.wireOp",EDGE,"E99"),sQuery(id+"F0.wireOp",EDGE,"E100"),sQuery(id+"F0.wireOp",EDGE,"E101"),sQuery(id+"F0.wireOp",EDGE,"E102"),sQuery(id+"F0.wireOp",EDGE,"E103"),sQuery(id+"F0.wireOp",EDGE,"E104"),sQuery(id+"F0.wireOp",EDGE,"E105"),sQuery(id+"F0.wireOp",EDGE,"E107"),sQuery(id+"F0.wireOp",EDGE,"E108"),sQuery(id+"F0.wireOp",EDGE,"E109"),sQuery(id+"F0.wireOp",EDGE,"E110"),sQuery(id+"F0.wireOp",EDGE,"E111"),sQuery(id+"F0.wireOp",EDGE,"E112"),sQuery(id+"F0.wireOp",EDGE,"E113"),sQuery(id+"F0.wireOp",EDGE,"E114"),sQuery(id+"F0.wireOp",EDGE,"E115")])]});
            var Q2;
            Q2=makeQuery(id+"F1.opExtrude","SWEPT_BODY",BODY,{"disambiguationData":[OSD([sQuery(id+"F0.wireOp",EDGE,"E6"),sQuery(id+"F0.wireOp",EDGE,"E7"),sQuery(id+"F0.wireOp",EDGE,"E8"),sQuery(id+"F0.wireOp",EDGE,"E9"),sQuery(id+"F0.wireOp",EDGE,"E10")])]});
            var Q3;
            Q3=makeQuery(id+"F1.opExtrude","SWEPT_BODY",BODY,{"disambiguationData":[OSD([sQuery(id+"F0.wireOp",EDGE,"E11"),sQuery(id+"F0.wireOp",EDGE,"E12"),sQuery(id+"F0.wireOp",EDGE,"E13"),sQuery(id+"F0.wireOp",EDGE,"E14"),sQuery(id+"F0.wireOp",EDGE,"E15"),sQuery(id+"F0.wireOp",EDGE,"E16"),sQuery(id+"F0.wireOp",EDGE,"E106")])]});
            var Q4;
            Q4=makeQuery(id+"F1.opExtrude","SWEPT_BODY",BODY,{"disambiguationData":[OSD([sQuery(id+"F0.wireOp",EDGE,"E17"),sQuery(id+"F0.wireOp",EDGE,"E18"),sQuery(id+"F0.wireOp",EDGE,"E19"),sQuery(id+"F0.wireOp",EDGE,"E20"),sQuery(id+"F0.wireOp",EDGE,"E21")])]});
            var Q5;
            Q5=makeQuery(id+"F1.opExtrude","SWEPT_BODY",BODY,{"disambiguationData":[OSD([sQuery(id+"F0.wireOp",EDGE,"E22"),sQuery(id+"F0.wireOp",EDGE,"E23"),sQuery(id+"F0.wireOp",EDGE,"E24"),sQuery(id+"F0.wireOp",EDGE,"E25"),sQuery(id+"F0.wireOp",EDGE,"E26"),sQuery(id+"F0.wireOp",EDGE,"E27"),sQuery(id+"F0.wireOp",EDGE,"E28"),sQuery(id+"F0.wireOp",EDGE,"E29"),sQuery(id+"F0.wireOp",EDGE,"E30"),sQuery(id+"F0.wireOp",EDGE,"E31"),sQuery(id+"F0.wireOp",EDGE,"E32"),sQuery(id+"F0.wireOp",EDGE,"E34"),sQuery(id+"F0.wireOp",EDGE,"E52.MirrorCS"),sQuery(id+"F0.wireOp",EDGE,"E53.MirrorCS"),sQuery(id+"F0.wireOp",EDGE,"E54.MirrorCS"),sQuery(id+"F0.wireOp",EDGE,"E55.MirrorCS"),sQuery(id+"F0.wireOp",EDGE,"E56.MirrorCS"),sQuery(id+"F0.wireOp",EDGE,"E57.MirrorCS"),sQuery(id+"F0.wireOp",EDGE,"E58.MirrorCS"),sQuery(id+"F0.wireOp",EDGE,"E59.MirrorCS"),sQuery(id+"F0.wireOp",EDGE,"E60.MirrorCS"),sQuery(id+"F0.wireOp",EDGE,"E61.MirrorCS"),sQuery(id+"F0.wireOp",EDGE,"E62.MirrorCS"),sQuery(id+"F0.wireOp",EDGE,"E63.MirrorCS")])]});
            var Q6;
            Q6=makeQuery(id+"F1.opExtrude","SWEPT_BODY",BODY,{"disambiguationData":[OSD([sQuery(id+"F0.wireOp",EDGE,"E35"),sQuery(id+"F0.wireOp",EDGE,"E36"),sQuery(id+"F0.wireOp",EDGE,"E37"),sQuery(id+"F0.wireOp",EDGE,"E38"),sQuery(id+"F0.wireOp",EDGE,"E39"),sQuery(id+"F0.wireOp",EDGE,"E40"),sQuery(id+"F0.wireOp",EDGE,"E41"),sQuery(id+"F0.wireOp",EDGE,"E42"),sQuery(id+"F0.wireOp",EDGE,"E43"),sQuery(id+"F0.wireOp",EDGE,"E44"),sQuery(id+"F0.wireOp",EDGE,"E45"),sQuery(id+"F0.wireOp",EDGE,"E46"),sQuery(id+"F0.wireOp",EDGE,"E47"),sQuery(id+"F0.wireOp",EDGE,"E48"),sQuery(id+"F0.wireOp",EDGE,"E49"),sQuery(id+"F0.wireOp",EDGE,"E50"),sQuery(id+"F0.wireOp",EDGE,"E51")])]});
            var Q7;
            Q7=makeQuery(id+"F1.opExtrude","SWEPT_BODY",BODY,{"disambiguationData":[OSD([sQuery(id+"F0.wireOp",EDGE,"E64.MirrorCS"),sQuery(id+"F0.wireOp",EDGE,"E65.MirrorCS"),sQuery(id+"F0.wireOp",EDGE,"E66.MirrorCS"),sQuery(id+"F0.wireOp",EDGE,"E67.MirrorCS"),sQuery(id+"F0.wireOp",EDGE,"E68.MirrorCS")])]});
            var Q8;
            Q8=makeQuery(id+"F1.opExtrude","SWEPT_BODY",BODY,{"disambiguationData":[OSD([sQuery(id+"F0.wireOp",EDGE,"E69.MirrorCS"),sQuery(id+"F0.wireOp",EDGE,"E70.MirrorCS"),sQuery(id+"F0.wireOp",EDGE,"E71.MirrorCS"),sQuery(id+"F0.wireOp",EDGE,"E72.MirrorCS"),sQuery(id+"F0.wireOp",EDGE,"E73.MirrorCS"),sQuery(id+"F0.wireOp",EDGE,"E74.MirrorCS"),sQuery(id+"F0.wireOp",EDGE,"E154.MirrorCS"),sQuery(id+"F0.wireOp",EDGE,"E155.MirrorCS"),sQuery(id+"F0.wireOp",EDGE,"E156.MirrorCS"),sQuery(id+"F0.wireOp",EDGE,"E157.MirrorCS"),sQuery(id+"F0.wireOp",EDGE,"E158.MirrorCS"),sQuery(id+"F0.wireOp",EDGE,"E159.MirrorCS"),sQuery(id+"F0.wireOp",EDGE,"E160.MirrorCS"),sQuery(id+"F0.wireOp",EDGE,"E161.MirrorCS"),sQuery(id+"F0.wireOp",EDGE,"E162.MirrorCS"),sQuery(id+"F0.wireOp",EDGE,"E163.MirrorCS"),sQuery(id+"F0.wireOp",EDGE,"E164.MirrorCS"),sQuery(id+"F0.wireOp",EDGE,"E165.MirrorCS"),sQuery(id+"F0.wireOp",EDGE,"E166.MirrorCS"),sQuery(id+"F0.wireOp",EDGE,"E167.MirrorCS"),sQuery(id+"F0.wireOp",EDGE,"E168.MirrorCS"),sQuery(id+"F0.wireOp",EDGE,"E169.MirrorCS"),sQuery(id+"F0.wireOp",EDGE,"E170.MirrorCS"),sQuery(id+"F0.wireOp",EDGE,"E171.MirrorCS"),sQuery(id+"F0.wireOp",EDGE,"E172.MirrorCS"),sQuery(id+"F0.wireOp",EDGE,"E173.MirrorCS"),sQuery(id+"F0.wireOp",EDGE,"E174.MirrorCS"),sQuery(id+"F0.wireOp",EDGE,"E175.MirrorCS"),sQuery(id+"F0.wireOp",EDGE,"E178.MirrorCS"),sQuery(id+"F0.wireOp",EDGE,"E179.MirrorCS"),sQuery(id+"F0.wireOp",EDGE,"E180.MirrorCS")])]});
            var Q9;
            Q9=makeQuery(id+"F1.opExtrude","SWEPT_BODY",BODY,{"disambiguationData":[OSD([sQuery(id+"F0.wireOp",EDGE,"E75.MirrorCS"),sQuery(id+"F0.wireOp",EDGE,"E76.MirrorCS"),sQuery(id+"F0.wireOp",EDGE,"E77.MirrorCS"),sQuery(id+"F0.wireOp",EDGE,"E78.MirrorCS"),sQuery(id+"F0.wireOp",EDGE,"E79.MirrorCS")])]});
            var Q10;
            Q10=makeQuery(id+"F1.opExtrude","SWEPT_BODY",BODY,{"disambiguationData":[OSD([sQuery(id+"F0.wireOp",EDGE,"E80.MirrorCS"),sQuery(id+"F0.wireOp",EDGE,"E81.MirrorCS"),sQuery(id+"F0.wireOp",EDGE,"E82.MirrorCS"),sQuery(id+"F0.wireOp",EDGE,"E83.MirrorCS"),sQuery(id+"F0.wireOp",EDGE,"E84.MirrorCS"),sQuery(id+"F0.wireOp",EDGE,"E85.MirrorCS"),sQuery(id+"F0.wireOp",EDGE,"E116"),sQuery(id+"F0.wireOp",EDGE,"E117")])]});
            var Q11;
            Q11=makeQuery(id+"F1.opExtrude","CAP_VERTEX",VERTEX,{"disambiguationData":[OSD([sQuery(id+"F0.wireOp",EDGE,"E74.MirrorCS"),sQuery(id+"F0.wireOp",EDGE,"E157.MirrorCS")])],"isStart":false});
            transform(context, id + "F2", {"entities" : qUnion([Q0, Q1, Q2, Q3, Q4, Q5, Q6, Q7, Q8, Q9, Q10]), "transformType" : TransformType.SCALE_UNIFORMLY, "scale" : 80 / 231, "scalePoint" : qUnion([Q11]), "makeCopy" : false});
        }
    });
